# Revit family: VLGFP1501-xxxSW8xxBxxxx
name_source: partatom
category: Leuchten
units: mm (PartAtom-declared; Revit-internal decimal feet)

## family parameters
Basisbauteil = Fläche
Beim Laden mit Abzugskörper schneiden = Nein
Bemaßung runder Anschluss = Durchmesser verwenden
Gemeinsam genutzt = Nein
Lichtquelle = Ja
OmniClass-Nummer = 23.80.70.11
OmniClass-Titel = Luminaries for Internal Lighting
Raumberechnungspunkt = Nein
Teiletyp = Normal

## types (12) — shared parameters
Baugruppenkennzeichen = D5020200
Datei für fotometrisches Netz = VLGFP1501-5NDWS840B0800.IES
Emissionsform beim Rendern sichtbar = Nein
Farbfilter = 16777215
Farbtemperaturverschiebung bei Dämpfen der Lampe = <Keine Auswahl>
Hersteller = RIDI Leuchten GmbH
Lampe = LED
Neigungswinkel = 90.00°
URL = www.ridi.de
Von Breite des Rechtecks ausssenden = 1469 mm  [stored 4.81955 ft]
Von Länge des Rechtecks aussenden = 63 mm  [stored 0.206693 ft]
brand = RIDI
conformity mark = CE
electrical safety class = 1
height = 66 mm  [stored 0.216535 ft]
ingress protection (IP) code = IP54
length = 1500 mm  [stored 4.92126 ft]
nominal frequency = 50-60Hz
nominal voltage = 230
voltage type (AC, DC, UC) = AC
weight = 1.9 kg
width = 67 mm
zero-valued in all types: Vorgabe-Ansicht

## per-type parameters (varying)
| type | Modell | Scheinlast | rated input power |
| VLGFP1501-5NDSW830B0750 | 1551029SW | 55 VA | 55 |
| VLGFP1501-7DASW830B0750 | 1561029SW | 55 VA | 55 |
| VLGFP1501-5NDSW830B0750-RF | 1551107SW | 55 VA | 55 |
| VLGFP1501-5NDSW840B0800 | 1551008SW | 55 VA | 55 |
| VLGFP1501-7DASW840B0800 | 1561008SW | 55 VA | 55 |
| VLGFP1501-5NDSW840B0800-RF | 1551103SW | 57 VA | 57 |
| VLGFP1501-5NDSW850B0850 | 1551043SW | 55 VA | 55 |
| VLGFP1501-7DASW850B0850 | 1561043SW | 55 VA | 55 |
| VLGFP1501-5NDSW850B0800-RF | 1551109SW | 55 VA | 55 |
| VLGFP1501-5NDSW865B0800 | 1551109SW | 55 VA | 55 |
| VLGFP1501-7DASW865B0800 | 1561056SW | 55 VA | 55 |
| VLGFP1501-5NDSW865B0800-RF | 1551105SW | 55 VA | 55 |

note: column(s) folded — value = type name in every type: product name

note: [stored X ft] marks values corroborated as IEEE doubles in the binary element streams (Revit-internal decimal feet)
